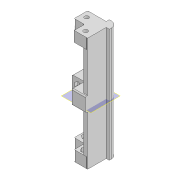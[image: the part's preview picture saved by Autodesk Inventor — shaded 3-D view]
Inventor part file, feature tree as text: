
AUTODESK INVENTOR PART (.ipt)
format: ipt  version: 2020 (Build 240168000, 168)  size: 350,208 bytes
history: native  units: mm
features: extrude x13, sketch x13, other x6, fillet x2
ambient origin geometry x8: Origin, YZ Plane, XZ Plane, XY Plane, X Axis, Y Axis, Z Axis, Center Point
bodies: Body1 (feature_tree)
feature tree (34):
  other  "Sólido1"
  extrude  "Extrusão1"  Depth=16.0mm
  extrude  "Extrusão2"  Depth=3.0mm
  extrude  "Extrusão3"  Depth=3.0mm
  extrude  "Extrusão4"  Depth=6.0mm
  extrude  "Extrusão5"  Depth=8.0mm
  fillet  "Arredondamento1"  Radius=110.0mm
  extrude  "Extrusão6"  Depth=10.0mm
  extrude  "Extrusão7"  TaperAngle=0.0deg  [1 undecoded]
  other  "Plano de trabalho1"
  extrude  "Extrusão9"  Depth=5.0mm
  extrude  "Extrusão10"  Depth=10.0mm
  extrude  "Extrusão11"  Depth=4.0mm
  extrude  "Extrusão12"  Depth=7.0mm
  extrude  "Extrusão13"  Depth=1.0mm TaperAngle=0.0deg
  fillet  "Arredondamento2"  Radius=1.0mm
  extrude  "Extrusão14"  Depth=6.8mm
  sketch  "Esboço1"  dims[d0=16.0mm d1=16.0mm]
  sketch  "Esboço2"  dims[d2=8.0mm d3=3.0mm]
  sketch  "Esboço3"  dims[d4=8.0mm d5=3.0mm]
  sketch  "Esboço4"  dims[d6=6.0mm d7=5.2mm]
  sketch  "Esboço5"  dims[d8=8.0mm d9=8.0mm d10=110.0mm d11=0.0mm]
  sketch  "Esboço6"  dims[d12=10.0mm d13=10.0mm]
  sketch  "Esboço7"  dims[d14=10.0mm d15=0.0mm d16=0.0mm]
  other  "Contorno projetado1"
  other  "Contorno projetado2"
  sketch  "Esboço9"  dims[d17=4.0mm d18=5.0mm]
  other  "Contorno projetado3"
  other  "Contorno projetado4"
  sketch  "Esboço10"  dims[d19=200.0mm d20=0.0mm d21=10.0mm]
  sketch  "Esboço11"  dims[d22=10.0mm d23=0.0mm d24=4.0mm]
  sketch  "Esboço12"  dims[d25=5.0mm d26=7.0mm]
  sketch  "Esboço13"  dims[d27=6.0mm d28=200.0mm d29=0.0mm d30=1.0mm]
  sketch  "Esboço14"  dims[d31=13.0mm d32=6.8mm d33=6.8mm d34=3.0mm d35=0.0mm d36=3.0mm d37=0.0mm d38=0.0mm d44=0.0mm d45=-50.0mm d46=12.0mm d47=12.0mm d48=2.0mm d49=0.0mm d50=12.0mm d51=0.0mm d52=4.5mm d53=6.0mm d54=20.0mm d55=0.0mm d56=4.5mm d57=6.0mm d58=20.0mm d59=0.0mm d60=6.8mm d61=3.0mm d62=0.0mm d63=6.8mm d64=3.0mm d65=0.0mm d66=1.0mm d67=4.0mm d68=0.0mm]
note: 1 required parameter value undecoded (feature->parameter linkage not recoverable at this tier; creation-order binding heuristic only, values carry confidence <= 0.55)
